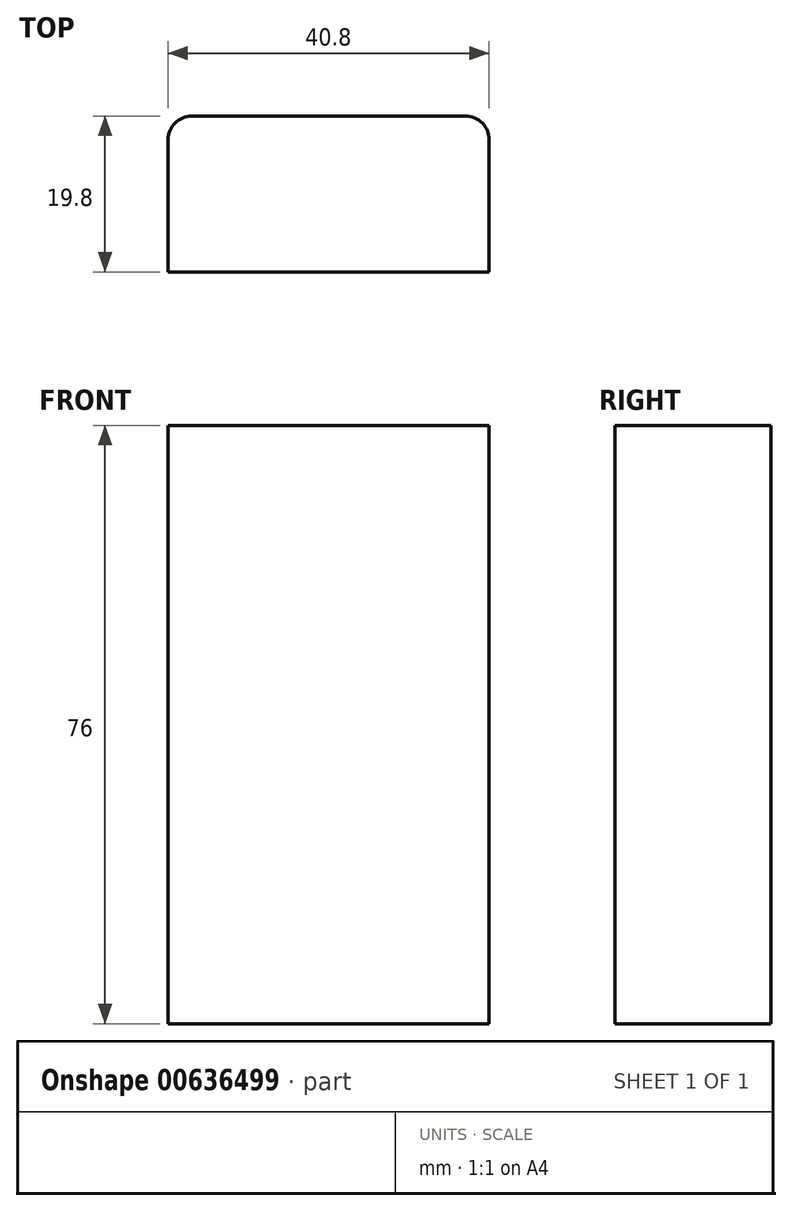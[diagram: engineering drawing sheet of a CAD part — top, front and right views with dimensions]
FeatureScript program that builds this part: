
annotation { "Feature Type Name" : "Feature", "Feature Type Description" : "" }
export const myFeature = defineFeature(function(context is Context, id is Id, definition is map)
    precondition{}
    {
        {
            var Q0;
            Q0=qCreatedBy(makeId("Top.planeOp"),FACE);
            var sketch = newSketch(context, id + "F0", { "sketchPlane" : qUnion([Q0])});
            skLineSegment(sketch, "E0.bottom", {"start": v(0, 0) * mm, "end": v(-40.8, 0) * mm});
            skLineSegment(sketch, "E0.top", {"start": v(-3, 19.8) * mm, "end": v(-37.8, 19.8) * mm});
            skLineSegment(sketch, "E0.left", {"start": v(0, 0) * mm, "end": v(0, 16.8) * mm});
            skLineSegment(sketch, "E0.right", {"start": v(-40.8, 0) * mm, "end": v(-40.8, 16.8) * mm});
            skPoint(sketch, "E1.visualSharp", {"position": v(-40.8, 19.8) * mm});
            skArc(sketch, "E1.filletArc", {"start": v(-37.8, 19.8) * mm, "mid": v(-39.92, 18.92) * mm, "end": v(-40.8, 16.8) * mm});
            skPoint(sketch, "E2.visualSharp", {"position": v(0, 19.8) * mm});
            skArc(sketch, "E2.filletArc", {"start": v(0, 16.8) * mm, "mid": v(-0.88, 18.92) * mm, "end": v(-3, 19.8) * mm});
            skSolve(sketch);
        }
        {
            var Q0;
            Q0=makeQuery(id+"F0.imprint","IMPRINT",FACE,{"disambiguationData":[TD([[makeQuery(id+"F0.imprint","IMPRINT",EDGE,{"derivedFrom":sQuery(id+"F0.wireOp",EDGE,"E0.bottom")}),-1.0]])]});
            extrude(context, id + "F1", {"entities" : qUnion([Q0]), "depth" : 76 * mm, "offsetDistance" : 25 * mm});
        }
    });
